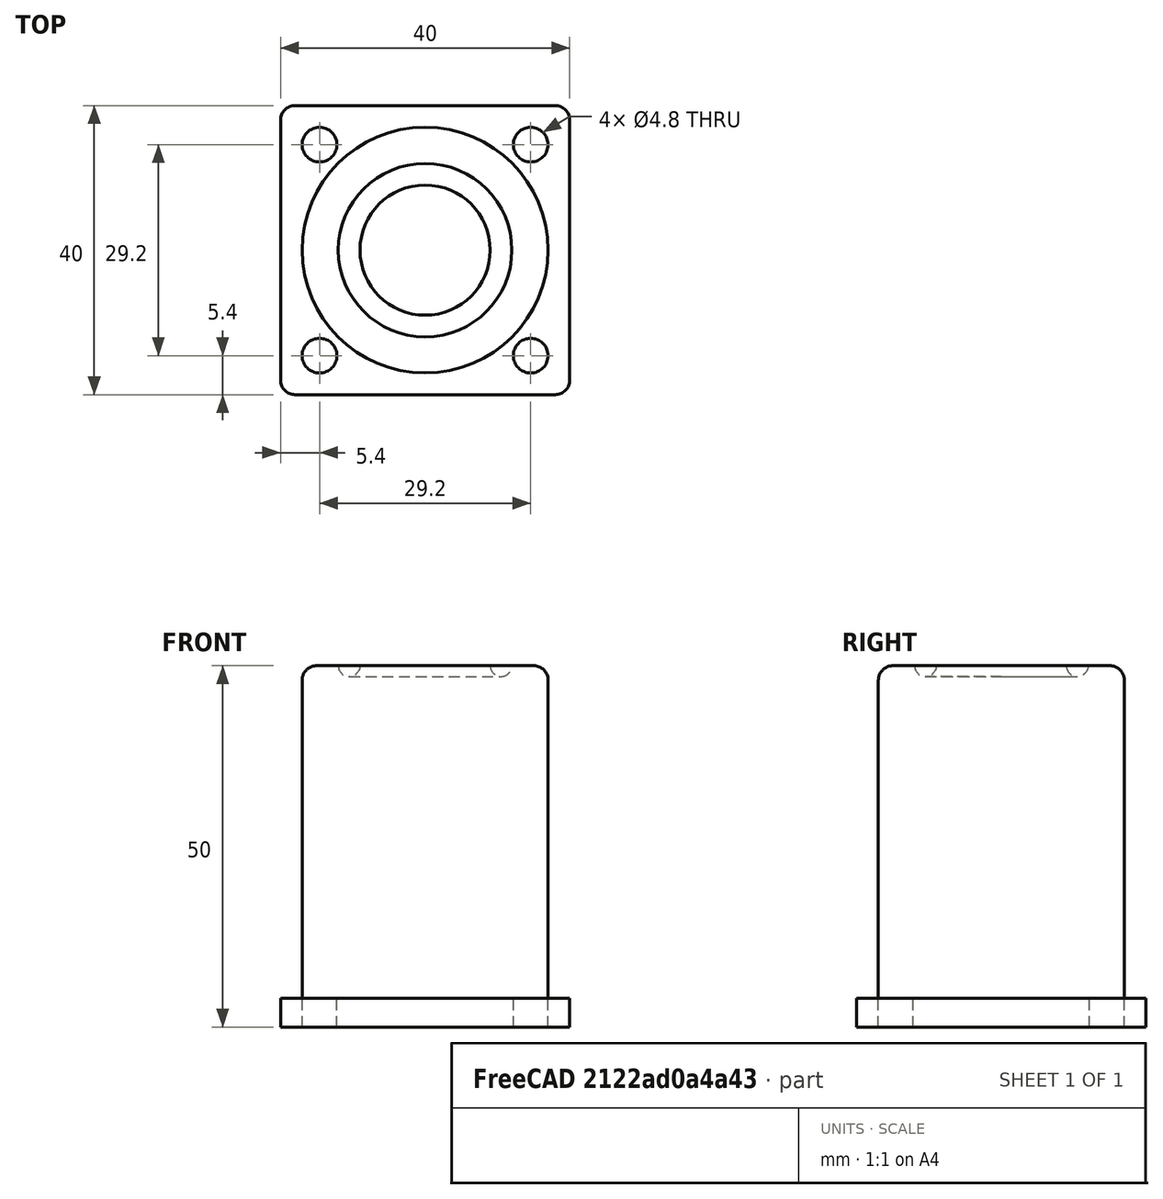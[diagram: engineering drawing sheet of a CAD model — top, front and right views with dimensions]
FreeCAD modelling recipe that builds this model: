
FCSTD DOCUMENT  (FreeCAD 0.18.4R)
Label: tutorial_freecad_ex15_d
License: All rights reserved
LicenseURL: http://en.wikipedia.org/wiki/All_rights_reserved
objects: Part::Cylinder×2, Part::Fillet×2, Part::Cut×2, Part::Box×1, Part::FeaturePython×1, Part::Torus×1, Part::MultiFuse×1
note: 10 computed .brp shape members not serialized (recipe doc carries the construction recipe); baked Part::Feature solids carry a one-line shape summary decoded from their .brp

FEATURE [Part::Box] Box  label="Cubo"
  AttacherType = Attacher::AttachEngine3D
  Height = 4
  Length = 40
  Width = 40
FEATURE [Part::Cylinder] Cylinder  label="taladros"
  Angle = 360
  AttacherType = Attacher::AttachEngine3D
  Height = 10
  Placement = pos=(5.4,5.4,0) rot=(0,0,1;0rad)
  Radius = 2.4
FEATURE [Part::FeaturePython] Array  label="taladros_vector"  # Draft array (typed FeaturePython)
  Angle = 360
  ArrayType = 0
  Axis = (0,0,1)
  Base = -> Cylinder
  Center = (0,0,0)
  Fuse = false
  IntervalAxis = (0,0,0)
  IntervalX = (29.2,0,0)
  IntervalY = (0,29.2,0)
  IntervalZ = (0,0,1)
  NumberPolar = 1
  NumberX = 2
  NumberY = 2
  NumberZ = 1
  Placement = pos=(0,0,-3) rot=(0,0,1;0rad)
FEATURE [Part::Fillet] Fillet  label="base_redondeada"
  Base = -> Box
  Edges = 4 edges r=2: [Edge1,Edge3,Edge5,Edge7]
FEATURE [Part::Cut] Cut  label="base_taladrada"
  Base = -> Fillet
  Refine = true
  Tool = -> Array
FEATURE [Part::Cylinder] Cylinder001  label="cilindro_base_pata"
  Angle = 360
  AttacherType = Attacher::AttachEngine3D
  Height = 50
  Radius = 17
FEATURE [Part::Torus] Torus  label="hueco_torica"
  Angle1 = -180
  Angle2 = 180
  Angle3 = 360
  AttacherType = Attacher::AttachEngine3D
  Placement = pos=(0,0,50) rot=(0,0,1;0rad)
  Radius1 = 10.5
  Radius2 = 1.5
FEATURE [Part::Fillet] Fillet001  label="cilindro_base_pata_redondeado"
  Base = -> Cylinder001
  Edges = 1 edges r=2: [Edge1]
FEATURE [Part::Cut] Cut001  label="base_pata_torica"
  Base = -> Fillet001
  Placement = pos=(20,20,0) rot=(0,0,1;0rad)
  Refine = true
  Tool = -> Torus
FEATURE [Part::MultiFuse] Fusion  label="pata_ikea"
  Refine = true
  Shapes = -> [Cut001,Cut]
